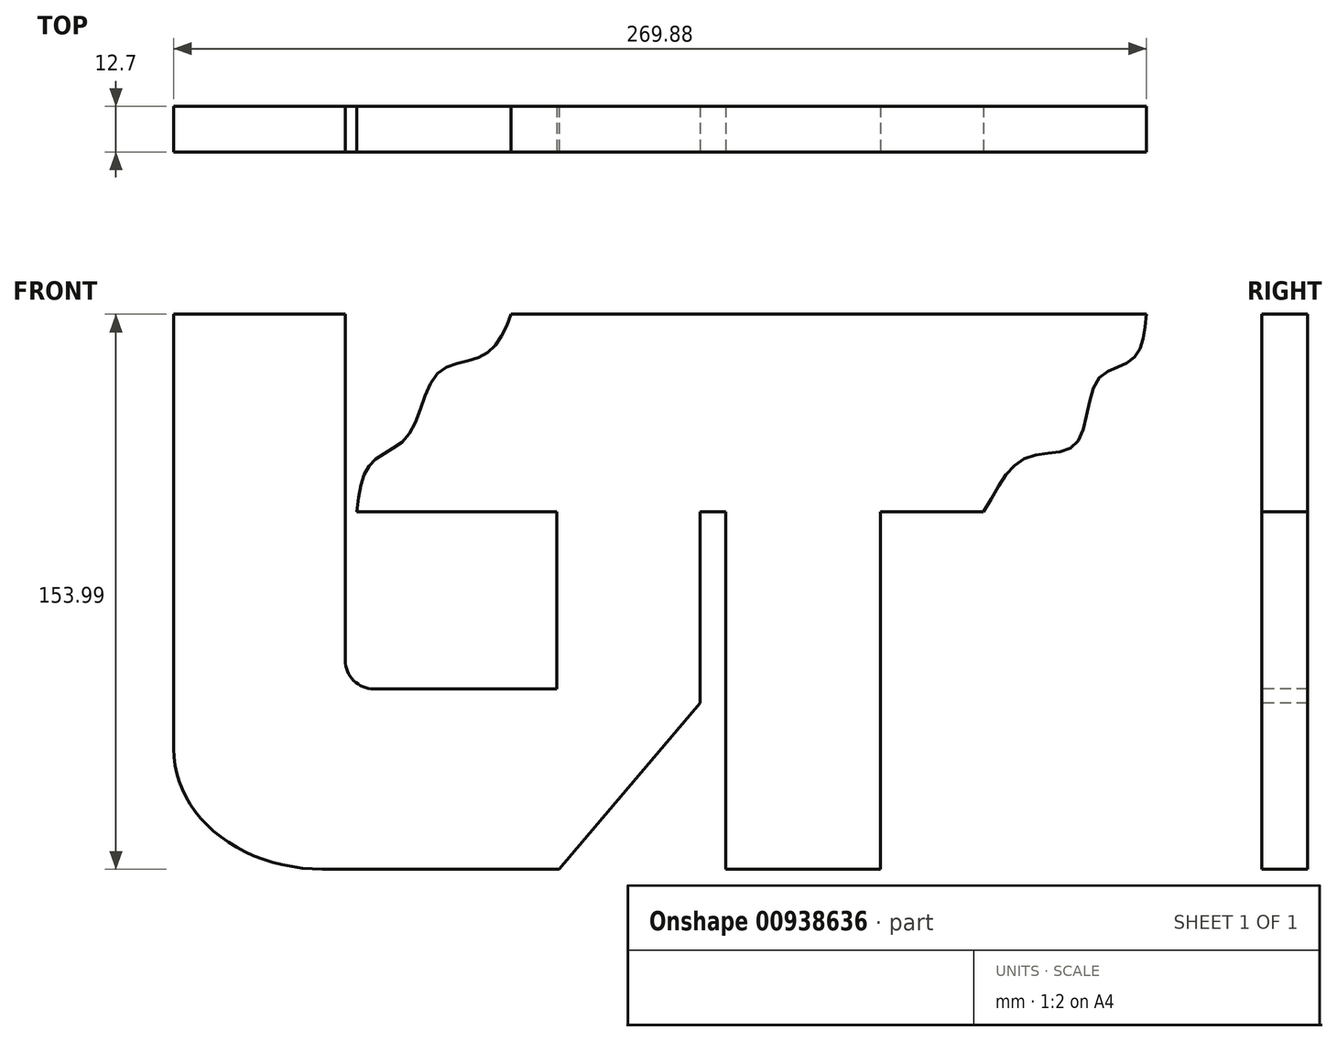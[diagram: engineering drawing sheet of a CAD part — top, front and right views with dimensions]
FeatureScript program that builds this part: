
annotation { "Feature Type Name" : "Feature", "Feature Type Description" : "" }
export const myFeature = defineFeature(function(context is Context, id is Id, definition is map)
    precondition{}
    {
        {
            var Q0;
            Q0=qCreatedBy(makeId("Front.planeOp"),FACE);
            var sketch = newSketch(context, id + "F0", { "sketchPlane" : qUnion([Q0])});
            skLineSegment(sketch, "E0", {"start": v(-55.27, 62.12) * mm, "end": v(-55.27, -58.53) * mm});
            skLineSegment(sketch, "E1", {"start": v(-14, -91.87) * mm, "end": v(51.62, -91.87) * mm});
            skLineSegment(sketch, "E2", {"start": v(-55.27, 62.12) * mm, "end": v(-7.64, 62.12) * mm});
            skLineSegment(sketch, "E3", {"start": v(-7.64, 62.12) * mm, "end": v(-7.64, -33.93) * mm});
            skLineSegment(sketch, "E4", {"start": v(0.3, -41.86) * mm, "end": v(51.1, -41.86) * mm});
            skLineSegment(sketch, "E5", {"start": v(51.1, -41.86) * mm, "end": v(51.1, 7.35) * mm});
            skLineSegment(sketch, "E6", {"start": v(51.1, 7.35) * mm, "end": v(-4.47, 7.35) * mm});
            skLineSegment(sketch, "E7", {"start": v(90.78, -45.83) * mm, "end": v(51.62, -91.87) * mm});
            skLineSegment(sketch, "E8", {"start": v(90.78, -45.83) * mm, "end": v(90.78, 7.35) * mm});
            skLineSegment(sketch, "E9", {"start": v(90.78, 7.35) * mm, "end": v(97.93, 7.35) * mm});
            skLineSegment(sketch, "E10", {"start": v(97.93, 7.35) * mm, "end": v(97.93, -91.87) * mm});
            skLineSegment(sketch, "E11", {"start": v(97.93, -91.87) * mm, "end": v(140.79, -91.87) * mm});
            skLineSegment(sketch, "E12", {"start": v(140.79, -91.87) * mm, "end": v(140.79, 7.35) * mm});
            skLineSegment(sketch, "E13", {"start": v(140.79, 7.35) * mm, "end": v(169.36, 7.35) * mm});
            skLineSegment(sketch, "E14", {"start": v(38.4, 62.12) * mm, "end": v(214.6, 62.12) * mm});
            skArc(sketch, "E15", {"start": v(-7.64, -33.93) * mm, "mid": v(-5.32, -39.54) * mm, "end": v(0.3, -41.86) * mm});
            skEllipticalArc(sketch, "E16", {});
            skFitSpline(sketch, "E17", {"points": [v(214.6, 62.12) * mm, v(210.9, 49.75) * mm, v(201.05, 43.87) * mm, v(194.98, 26.05) * mm, v(181.14, 22.26) * mm, v(169.36, 7.35) * mm], "startDerivative": vector(-7.34, -79.97) * mm, "endDerivative": vector(-51.67, -81.86) * mm});
            skFitSpline(sketch, "E18", {"points": [v(38.4, 62.12) * mm, v(30.78, 50.8) * mm, v(18.15, 45.84) * mm, v(9.8, 28.48) * mm, v(0, 21.27) * mm, v(-4.47, 7.35) * mm], "startDerivative": vector(-27.28, -74.31) * mm, "endDerivative": vector(-9.34, -92.98) * mm});
            const initialGuessF0  = {"E16": [-0.013992572402954088, -0.058531753283739094, 0, -1, 0.033337500000000006, 0.041275, 4.71238898038469, 6.283185307179586]};
            skSetInitialGuess(sketch, initialGuessF0);
            skSolve(sketch);
        }
        {
            var Q0;
            Q0=makeQuery(id+"F0.imprint","IMPRINT",FACE,{"disambiguationData":[TD([[makeQuery(id+"F0.imprint","IMPRINT",EDGE,{"derivedFrom":sQuery(id+"F0.wireOp",EDGE,"E0")}),1.0]])]});
            extrude(context, id + "F1", {"entities" : qUnion([Q0]), "oppositeDirection" : true, "depth" : 12.7 * mm, "offsetDistance" : 25.4 * mm});
        }
    });
